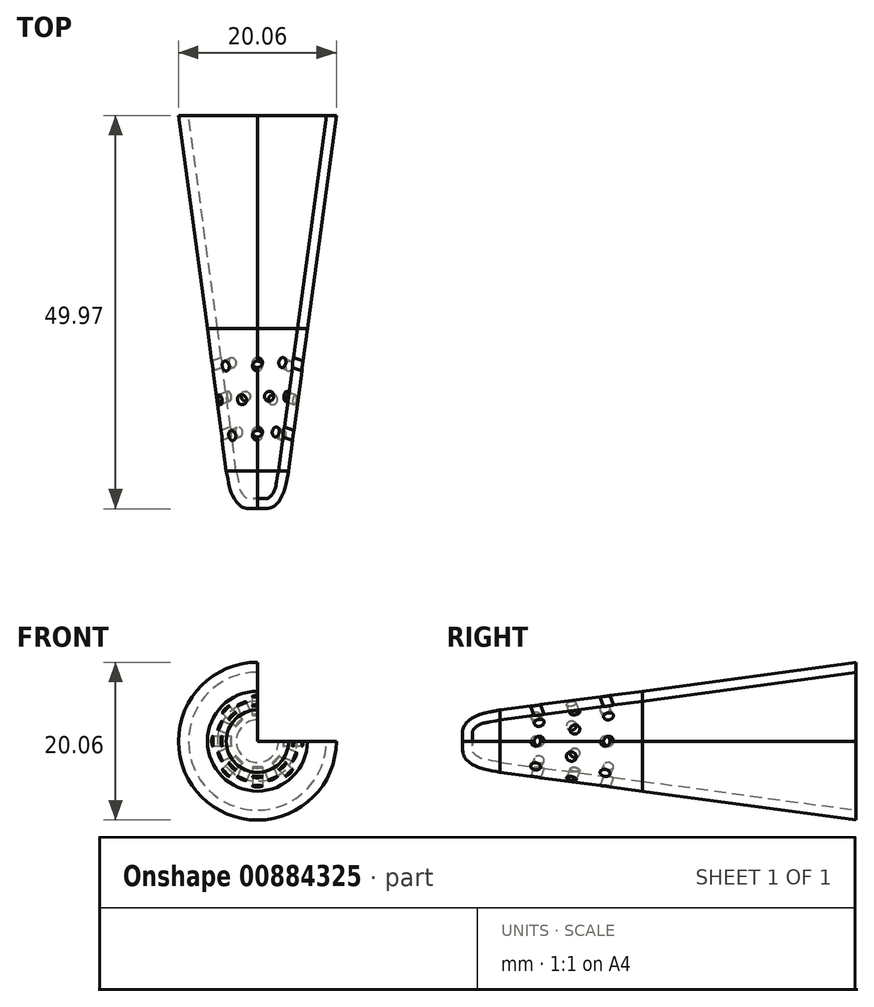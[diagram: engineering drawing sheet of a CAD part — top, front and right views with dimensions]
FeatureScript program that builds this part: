
annotation { "Feature Type Name" : "Feature", "Feature Type Description" : "" }
export const myFeature = defineFeature(function(context is Context, id is Id, definition is map)
    precondition{}
    {
        {
            var Q0;
            Q0=qCreatedBy(makeId("Right.planeOp"),FACE);
            var sketch = newSketch(context, id + "F0", { "sketchPlane" : qUnion([Q0])});
            skFitSpline(sketch, "E0", {"points": [v(0, 0) * mm, v(0, 1.1) * mm, v(0.45, 2.3) * mm, v(2.09, 3.34) * mm, v(4.76, 3.97) * mm], "startDerivative": vector(-0.16, 5.28) * mm, "endDerivative": vector(14.36, 3.06) * mm});
            skLineSegment(sketch, "E1", {"start": v(4.76, 3.97) * mm, "end": v(22.86, 6.35) * mm});
            skLineSegment(sketch, "E2", {"start": v(22.86, 6.35) * mm, "end": v(22.86, 0) * mm});
            skLineSegment(sketch, "E3", {"start": v(22.86, 0) * mm, "end": v(0, 0) * mm});
            skLineSegment(sketch, "E4", {"start": v(0, 0) * mm, "end": v(44.4, 0) * mm, "construction": true});
            skFitSpline(sketch, "E5", {"points": [v(1.27, 0) * mm, v(1.27, 1.1) * mm, v(1.34, 1.4) * mm, v(2.09, 2.07) * mm, v(4.76, 2.69) * mm], "startDerivative": vector(-0.16, 5.28) * mm, "endDerivative": vector(14.36, 3.06) * mm});
            skLineSegment(sketch, "E6", {"start": v(4.76, 2.69) * mm, "end": v(22.86, 5.08) * mm});
            skLineSegment(sketch, "E7", {"start": v(4.76, 3.97) * mm, "end": v(4.76, 2.69) * mm});
            skSolve(sketch);
        }
        {
            var Q0;
            {var subQ4=sQuery(id+"F0.wireOp",EDGE,"E0");Q0=makeQuery(id+"F0.imprint","IMPRINT",FACE,{"disambiguationData":[TD([[makeQuery(id+"F0.imprint","IMPRINT",EDGE,{"derivedFrom":subQ4}),-1.0]])]});}
            var Q1;
            Q1=sQuery(id+"F0.wireOp",EDGE,"E4");
            revolve(context, id + "F1", {"surfaceOperationType" : NewSurfaceOperationType.NEW, "entities" : qUnion([Q0]), "axis" : qUnion([Q1]), "revolveType" : RevolveType.FULL});
        }
        {
            var Q0;
            Q0=qCreatedBy(makeId("Right.planeOp"),FACE);
            var sketch = newSketch(context, id + "F2", { "sketchPlane" : qUnion([Q0])});
            skLineSegment(sketch, "E8", {"start": v(0, 0) * mm, "end": v(22.86, 0) * mm});
            skLineSegment(sketch, "E9", {"start": v(22.86, 0) * mm, "end": v(22.86, 6.35) * mm});
            skLineSegment(sketch, "E10", {"start": v(22.86, 6.35) * mm, "end": v(49.95, 10.03) * mm});
            skLineSegment(sketch, "E11", {"start": v(49.95, 10.03) * mm, "end": v(49.95, 0) * mm});
            skLineSegment(sketch, "E12", {"start": v(49.95, 0) * mm, "end": v(22.86, 0) * mm});
            skLineSegment(sketch, "E13", {"start": v(22.86, 6.35) * mm, "end": v(22.86, 5.08) * mm});
            skLineSegment(sketch, "E14", {"start": v(22.86, 5.08) * mm, "end": v(49.95, 8.76) * mm});
            skLineSegment(sketch, "E15", {"start": v(49.95, 8.76) * mm, "end": v(49.95, 10.03) * mm});
            skSolve(sketch);
        }
        {
            var Q0;
            {var subQ0=sQuery(id+"F2.wireOp",EDGE,"E10");Q0=makeQuery(id+"F2.imprint","IMPRINT",FACE,{"disambiguationData":[TD([[makeQuery(id+"F2.imprint","IMPRINT",EDGE,{"derivedFrom":subQ0}),-1.0]])]});}
            var Q1;
            Q1=sQuery(id+"F2.wireOp",EDGE,"E12");
            revolve(context, id + "F3", {"operationType" : NewBodyOperationType.ADD, "surfaceOperationType" : NewSurfaceOperationType.NEW, "entities" : qUnion([Q0]), "axis" : qUnion([Q1]), "revolveType" : RevolveType.FULL});
        }
        {
            var Q0;
            {var subQ0=sQuery(id+"F0.wireOp",EDGE,"E1");Q0=makeQuery(id+"F0.imprint","IMPRINT",FACE,{"disambiguationData":[TD([[makeQuery(id+"F0.imprint","IMPRINT",EDGE,{"derivedFrom":subQ0}),-1.0]])]});}
            var Q1;
            Q1=sQuery(id+"F0.wireOp",EDGE,"E3");
            revolve(context, id + "F4", {"surfaceOperationType" : NewSurfaceOperationType.NEW, "entities" : qUnion([Q0]), "axis" : qUnion([Q1]), "revolveType" : RevolveType.FULL});
        }
        {
            var Q0;
            Q0=sQuery(id+"F0.wireOp",EDGE,"E1");
            cPlane(context, id + "F5", {"entities" : qUnion([Q0]), "cplaneType" : CPlaneType.LINE_ANGLE, "offset" : 25.4 * mm, "angle" : 0 * degree, "width" : 152.4 * mm, "height" : 152.4 * mm});
        }
        {
            var Q0;
            Q0=qCreatedBy(id+"F5.planeOp",FACE);
            var sketch = newSketch(context, id + "F6", { "sketchPlane" : qUnion([Q0])});
            skCircle(sketch, "E16", {"center": v(0, 9.8) * mm, "radius": 0.64 * mm});
            skCircle(sketch, "E17", {"center": v(0, 18.7) * mm, "radius": 0.64 * mm});
            skLineSegment(sketch, "E18", {"start": v(0, 5.23) * mm, "end": v(0, 23.5) * mm});
            skSolve(sketch);
        }
        {
            var Q0;
            Q0=qCreatedBy(makeId("Right.planeOp"),FACE);
            var sketch = newSketch(context, id + "F7", { "sketchPlane" : qUnion([Q0])});
            skLineSegment(sketch, "E19", {"start": v(9.29, 4.57) * mm, "end": v(9.81, 3.13) * mm});
            skLineSegment(sketch, "E20", {"start": v(9.29, 4.57) * mm, "end": v(9.29, 0) * mm, "construction": true});
            skLineSegment(sketch, "E21", {"start": v(18.1, 5.72) * mm, "end": v(18.62, 4.3) * mm});
            skLineSegment(sketch, "E22", {"start": v(18.1, 5.72) * mm, "end": v(18.1, 0) * mm, "construction": true});
            skSolve(sketch);
        }
        {
            var Q0;
            {var subQ0=sQuery(id+"F6.wireOp",EDGE,"E18");var subQ1=sQuery(id+"F6.wireOp",EDGE,"E16");var subQ2=makeQuery(id+"F6.imprint","INTERSECT",VERTEX,{"disambiguationData":[OD(0.0)],"derivedFrom":[subQ1,subQ0]});Q0=makeQuery(id+"F6.imprint","IMPRINT",FACE,{"disambiguationData":[TD([[makeQuery(id+"F6.imprint","IMPRINT",EDGE,{"disambiguationData":[TD([[subQ2,1.0]])],"derivedFrom":subQ1}),1.0]])]});}
            var Q1;
            {var subQ0=sQuery(id+"F6.wireOp",EDGE,"E18");var subQ1=sQuery(id+"F6.wireOp",EDGE,"E16");var subQ2=makeQuery(id+"F6.imprint","INTERSECT",VERTEX,{"disambiguationData":[OD(0.0)],"derivedFrom":[subQ1,subQ0]});Q1=makeQuery(id+"F6.imprint","IMPRINT",FACE,{"disambiguationData":[TD([[makeQuery(id+"F6.imprint","IMPRINT",EDGE,{"disambiguationData":[TD([[subQ2,-1.0]])],"derivedFrom":subQ1}),1.0]])]});}
            var Q2;
            Q2=sQuery(id+"F7.wireOp",EDGE,"E19");
            sweep(context, id + "F8", {"profiles" : qUnion([Q0, Q1]), "path" : qUnion([Q2])});
        }
        {
            var Q0;
            {var subQ0=sQuery(id+"F6.wireOp",EDGE,"E18");var subQ1=sQuery(id+"F6.wireOp",EDGE,"E17");var subQ2=makeQuery(id+"F6.imprint","INTERSECT",VERTEX,{"disambiguationData":[OD(0.0)],"derivedFrom":[subQ1,subQ0]});Q0=makeQuery(id+"F6.imprint","IMPRINT",FACE,{"disambiguationData":[TD([[makeQuery(id+"F6.imprint","IMPRINT",EDGE,{"disambiguationData":[TD([[subQ2,1.0]])],"derivedFrom":subQ1}),1.0]])]});}
            var Q1;
            {var subQ0=sQuery(id+"F6.wireOp",EDGE,"E18");var subQ1=sQuery(id+"F6.wireOp",EDGE,"E17");var subQ2=makeQuery(id+"F6.imprint","INTERSECT",VERTEX,{"disambiguationData":[OD(0.0)],"derivedFrom":[subQ1,subQ0]});Q1=makeQuery(id+"F6.imprint","IMPRINT",FACE,{"disambiguationData":[TD([[makeQuery(id+"F6.imprint","IMPRINT",EDGE,{"disambiguationData":[TD([[subQ2,-1.0]])],"derivedFrom":subQ1}),1.0]])]});}
            var Q2;
            Q2=sQuery(id+"F7.wireOp",EDGE,"E21");
            sweep(context, id + "F9", {"profiles" : qUnion([Q0, Q1]), "path" : qUnion([Q2])});
        }
        {
            var Q0;
            Q0=makeQuery(id+"F8.opSweep","SWEPT_BODY",BODY,{"disambiguationData":[OSD([sQuery(id+"F6.wireOp",EDGE,"E16"),sQuery(id+"F7.wireOp",EDGE,"E19")])]});
            var Q1;
            Q1=makeQuery(id+"F9.opSweep","SWEPT_BODY",BODY,{"disambiguationData":[OSD([sQuery(id+"F6.wireOp",EDGE,"E17"),sQuery(id+"F7.wireOp",EDGE,"E21")])]});
            var Q2;
            Q2=makeQuery(id+"F4.opRevolve","SWEPT_EDGE",EDGE,{"disambiguationData":[OSD([sQuery(id+"F0.wireOp",EDGE,"E1"),sQuery(id+"F0.wireOp",EDGE,"E2")])]});
            var Q3;
            Q3=makeQuery(id+"F4.opRevolve","SWEPT_BODY",BODY,{"disambiguationData":[OSD([sQuery(id+"F0.wireOp",EDGE,"E1"),sQuery(id+"F0.wireOp",EDGE,"E2"),sQuery(id+"F0.wireOp",EDGE,"E6"),sQuery(id+"F0.wireOp",EDGE,"E7")])]});
            circularPattern(context, id + "F10", {"operationType" : NewBodyOperationType.REMOVE, "entities" : qUnion([Q0, Q1]), "axis" : qUnion([Q2]), "angle" : 360 * degree, "instanceCount" : 8, "equalSpace" : true, "isCentered" : true});
        }
        {
            var Q0;
            Q0=sQuery(id+"F0.wireOp",EDGE,"E4");
            cPlane(context, id + "F11", {"entities" : qUnion([Q0]), "cplaneType" : CPlaneType.LINE_ANGLE, "offset" : 25.4 * mm, "angle" : 22.5 * degree, "width" : 152.4 * mm, "height" : 152.4 * mm});
        }
        {
            var Q0;
            Q0=qCreatedBy(id+"F11.planeOp",FACE);
            var sketch = newSketch(context, id + "F12", { "sketchPlane" : qUnion([Q0])});
            skLineSegment(sketch, "E23", {"start": v(-6.35, 22.86) * mm, "end": v(-3.97, 4.76) * mm});
            skLineSegment(sketch, "E24", {"start": v(3.97, 4.76) * mm, "end": v(6.35, 22.86) * mm});
            skSolve(sketch);
        }
        {
            var Q0;
            Q0=sQuery(id+"F12.wireOp",EDGE,"E23");
            cPlane(context, id + "F13", {"entities" : qUnion([Q0]), "cplaneType" : CPlaneType.LINE_ANGLE, "offset" : 25.4 * mm, "angle" : 67.5 * degree, "width" : 152.4 * mm, "height" : 152.4 * mm});
        }
        {
            var Q0;
            Q0=qCreatedBy(id+"F13.planeOp",FACE);
            var sketch = newSketch(context, id + "F14", { "sketchPlane" : qUnion([Q0])});
            skLineSegment(sketch, "E25", {"start": v(23.5, 0.02) * mm, "end": v(5.23, 0.01) * mm, "construction": true});
            skCircle(sketch, "E26", {"center": v(14.38, 0.02) * mm, "radius": 0.64 * mm});
            skSolve(sketch);
        }
        {
            var Q0;
            Q0=qCreatedBy(id+"F11.planeOp",FACE);
            var sketch = newSketch(context, id + "F15", { "sketchPlane" : qUnion([Q0])});
            skLineSegment(sketch, "E27", {"start": v(-5.16, 13.82) * mm, "end": v(-3.73, 14.34) * mm});
            skLineSegment(sketch, "E28", {"start": v(-5.16, 13.82) * mm, "end": v(0, 13.82) * mm});
            skLineSegment(sketch, "E29", {"start": v(-3.73, 14.34) * mm, "end": v(-6.51, 13.33) * mm});
            skSolve(sketch);
        }
        {
            var Q0;
            Q0=makeQuery(id+"F14.imprint","IMPRINT",FACE,{"disambiguationData":[TD([[makeQuery(id+"F14.imprint","IMPRINT",EDGE,{"derivedFrom":sQuery(id+"F14.wireOp",EDGE,"E26")}),1.0]])]});
            var Q1;
            Q1=sQuery(id+"F15.wireOp",EDGE,"E29");
            sweep(context, id + "F16", {"profiles" : qUnion([Q0]), "path" : qUnion([Q1])});
        }
        {
            var Q0;
            Q0=makeQuery(id+"F16.opSweep","SWEPT_BODY",BODY,{"disambiguationData":[OSD([sQuery(id+"F14.wireOp",EDGE,"E26"),sQuery(id+"F15.wireOp",EDGE,"E27")])]});
            var Q1;
            Q1=makeQuery(id+"F3.opRevolve","SWEPT_EDGE",EDGE,{"disambiguationData":[OSD([sQuery(id+"F2.wireOp",EDGE,"E9"),sQuery(id+"F2.wireOp",EDGE,"E10")])]});
            circularPattern(context, id + "F17", {"operationType" : NewBodyOperationType.REMOVE, "entities" : qUnion([Q0]), "axis" : qUnion([Q1]), "angle" : 360 * degree, "instanceCount" : 8, "equalSpace" : true});
        }
        {
            var Q0;
            Q0=qCreatedBy(makeId("Right.planeOp"),FACE);
            var sketch = newSketch(context, id + "F18", { "sketchPlane" : qUnion([Q0])});
            skLineSegment(sketch, "E30.bottom", {"start": v(-2.98, 0) * mm, "end": v(62.48, 0) * mm});
            skLineSegment(sketch, "E30.top", {"start": v(-2.98, 18.36) * mm, "end": v(62.48, 18.36) * mm});
            skLineSegment(sketch, "E30.left", {"start": v(-2.98, 0) * mm, "end": v(-2.98, 18.36) * mm});
            skLineSegment(sketch, "E30.right", {"start": v(62.48, 0) * mm, "end": v(62.48, 18.36) * mm});
            skSolve(sketch);
        }
        {
            var Q0;
            Q0=makeQuery(id+"F18.imprint","IMPRINT",FACE,{"disambiguationData":[TD([[makeQuery(id+"F18.imprint","IMPRINT",EDGE,{"derivedFrom":sQuery(id+"F18.wireOp",EDGE,"E30.bottom")}),1.0]])]});
            extrude(context, id + "F19", {"entities" : qUnion([Q0]), "operationType" : NewBodyOperationType.REMOVE, "depth" : 25.4 * mm, "offsetDistance" : 25.4 * mm});
        }
    });
